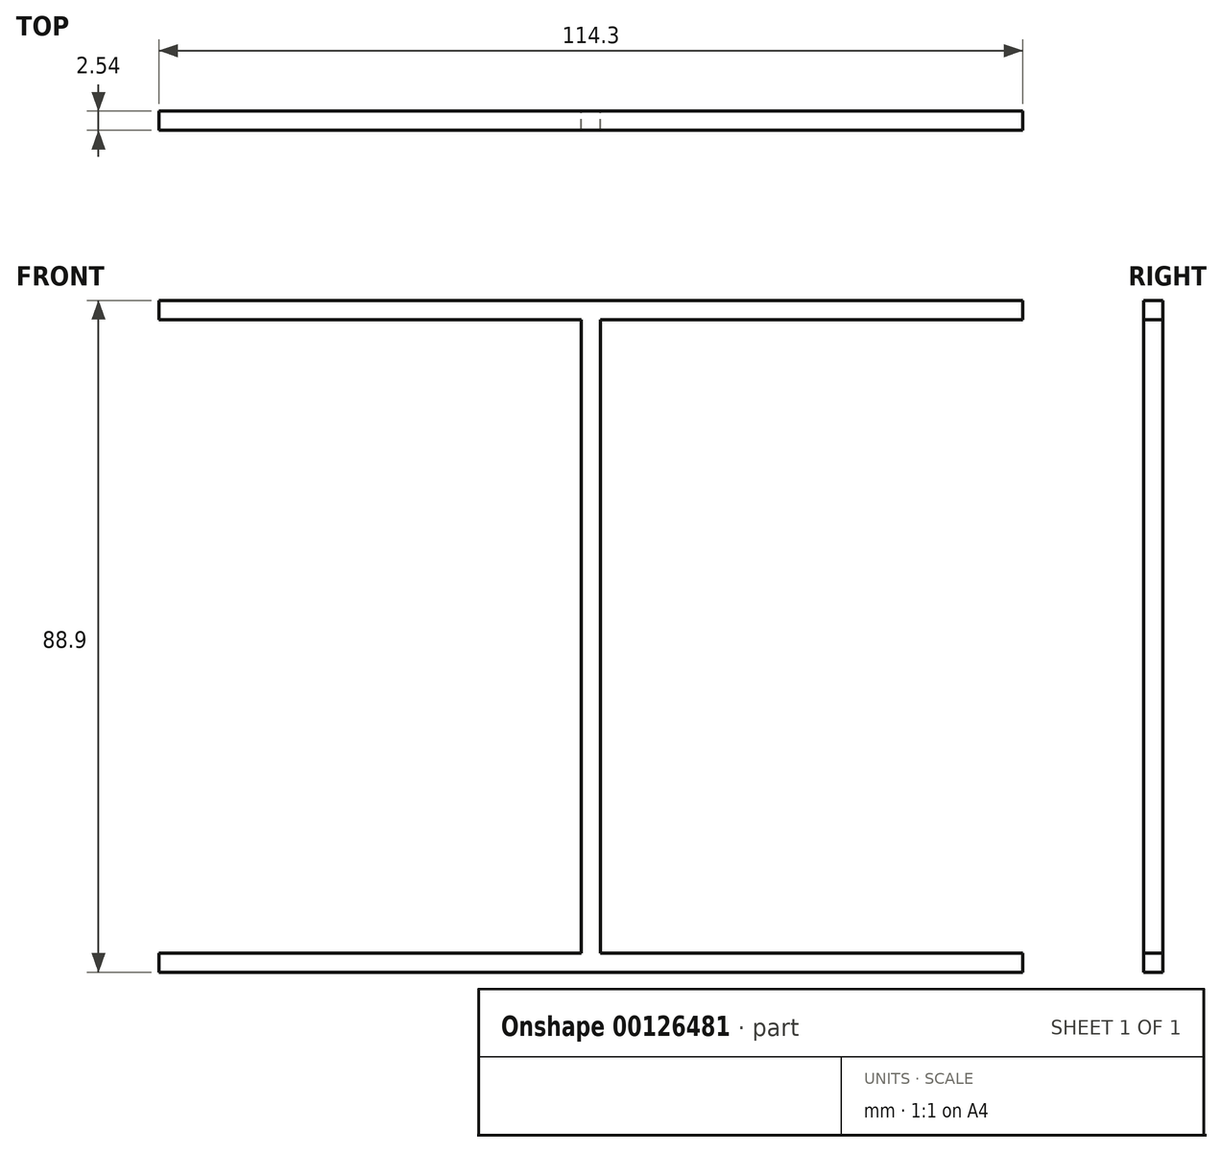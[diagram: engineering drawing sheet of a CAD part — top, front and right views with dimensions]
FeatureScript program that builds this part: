
annotation { "Feature Type Name" : "Feature", "Feature Type Description" : "" }
export const myFeature = defineFeature(function(context is Context, id is Id, definition is map)
    precondition{}
    {
        {
            var Q0;
            Q0=qCreatedBy(makeId("Front.planeOp"),FACE);
            var sketch = newSketch(context, id + "F0", { "sketchPlane" : qUnion([Q0])});
            skLineSegment(sketch, "E0", {"start": v(-1.27, -36.1) * mm, "end": v(-1.27, 47.72) * mm});
            skLineSegment(sketch, "E1", {"start": v(1.27, 47.72) * mm, "end": v(1.27, -36.1) * mm});
            skLineSegment(sketch, "E2", {"start": v(-1.27, 47.72) * mm, "end": v(-57.15, 47.72) * mm});
            skLineSegment(sketch, "E3", {"start": v(1.27, 47.72) * mm, "end": v(57.15, 47.72) * mm});
            skLineSegment(sketch, "E4", {"start": v(-57.15, 47.72) * mm, "end": v(-57.15, 50.26) * mm});
            skLineSegment(sketch, "E5", {"start": v(57.15, 47.72) * mm, "end": v(57.15, 50.26) * mm});
            skLineSegment(sketch, "E6", {"start": v(57.15, 50.26) * mm, "end": v(-57.15, 50.26) * mm});
            skLineSegment(sketch, "E7", {"start": v(-1.27, -36.1) * mm, "end": v(-57.15, -36.1) * mm});
            skLineSegment(sketch, "E8", {"start": v(1.27, -36.1) * mm, "end": v(57.15, -36.1) * mm});
            skLineSegment(sketch, "E9", {"start": v(-57.15, -36.1) * mm, "end": v(-57.15, -38.64) * mm});
            skLineSegment(sketch, "E10", {"start": v(57.15, -36.1) * mm, "end": v(57.15, -38.64) * mm});
            skLineSegment(sketch, "E11", {"start": v(-57.15, -38.64) * mm, "end": v(57.15, -38.64) * mm});
            skSolve(sketch);
        }
        {
            var Q0;
            Q0 = qSketchRegion(id + "F0", true);
            extrude(context, id + "F1", {"entities" : qUnion([Q0]), "depth" : 2.54 * mm});
        }
    });
